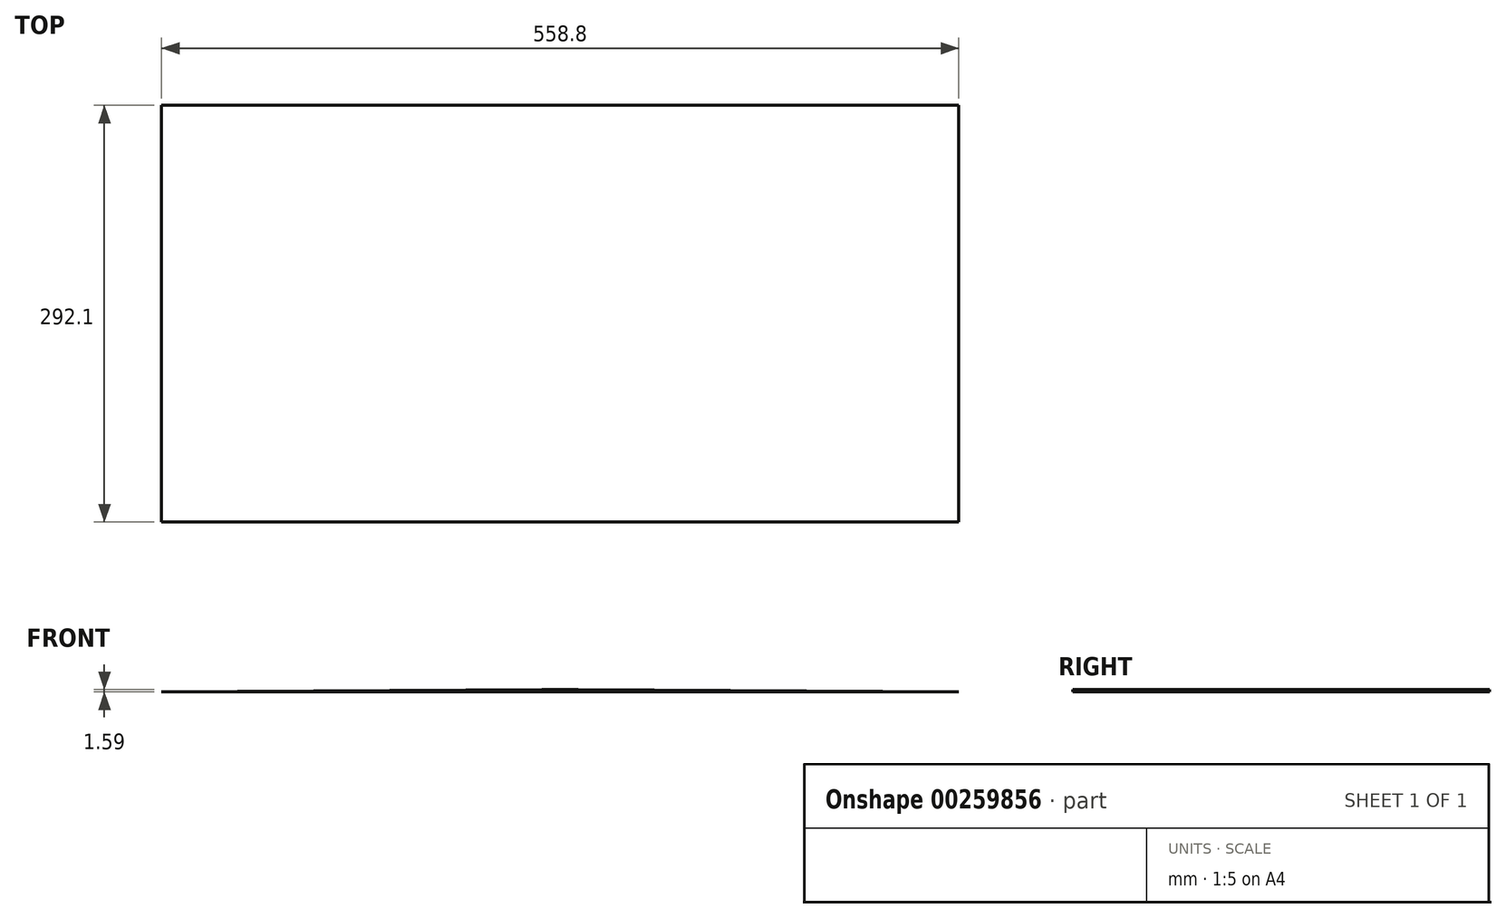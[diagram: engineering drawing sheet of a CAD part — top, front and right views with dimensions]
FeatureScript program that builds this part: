
annotation { "Feature Type Name" : "Feature", "Feature Type Description" : "" }
export const myFeature = defineFeature(function(context is Context, id is Id, definition is map)
    precondition{}
    {
        {
            var Q0;
            Q0=qCreatedBy(makeId("Front.planeOp"),FACE);
            var sketch = newSketch(context, id + "F0", { "sketchPlane" : qUnion([Q0])});
            skLineSegment(sketch, "E0", {"start": v(-42.83, 18.47) * mm, "end": v(223.87, 20.06) * mm});
            skLineSegment(sketch, "E1", {"start": v(223.87, 20.06) * mm, "end": v(223.87, 18.47) * mm});
            skLineSegment(sketch, "E2", {"start": v(223.87, 18.47) * mm, "end": v(-42.83, 18.47) * mm});
            skLineSegment(sketch, "E3", {"start": v(223.87, 18.47) * mm, "end": v(249.27, 18.47) * mm});
            skLineSegment(sketch, "E4", {"start": v(249.27, 18.47) * mm, "end": v(249.27, 20.06) * mm});
            skLineSegment(sketch, "E5", {"start": v(249.27, 20.06) * mm, "end": v(223.87, 20.06) * mm});
            skLineSegment(sketch, "E6", {"start": v(249.27, 20.06) * mm, "end": v(515.97, 18.47) * mm});
            skLineSegment(sketch, "E7", {"start": v(515.97, 18.47) * mm, "end": v(249.27, 18.47) * mm});
            skSolve(sketch);
        }
        {
            var Q0;
            Q0=makeQuery(id+"F0.imprint","IMPRINT",FACE,{"disambiguationData":[TD([[makeQuery(id+"F0.imprint","IMPRINT",EDGE,{"derivedFrom":sQuery(id+"F0.wireOp",EDGE,"E0")}),-1.0]])]});
            var Q1;
            Q1=makeQuery(id+"F0.imprint","IMPRINT",FACE,{"disambiguationData":[TD([[makeQuery(id+"F0.imprint","IMPRINT",EDGE,{"derivedFrom":sQuery(id+"F0.wireOp",EDGE,"E4")}),-1.0]])]});
            extrude(context, id + "F1", {"entities" : qUnion([Q0, Q1]), "depth" : 292.1 * mm});
        }
        {
            var Q0;
            Q0=makeQuery(id+"F0.imprint","IMPRINT",FACE,{"disambiguationData":[TD([[makeQuery(id+"F0.imprint","IMPRINT",EDGE,{"derivedFrom":sQuery(id+"F0.wireOp",EDGE,"E1")}),1.0]])]});
            extrude(context, id + "F2", {"entities" : qUnion([Q0]), "operationType" : NewBodyOperationType.ADD, "depth" : 292.1 * mm});
        }
    });
